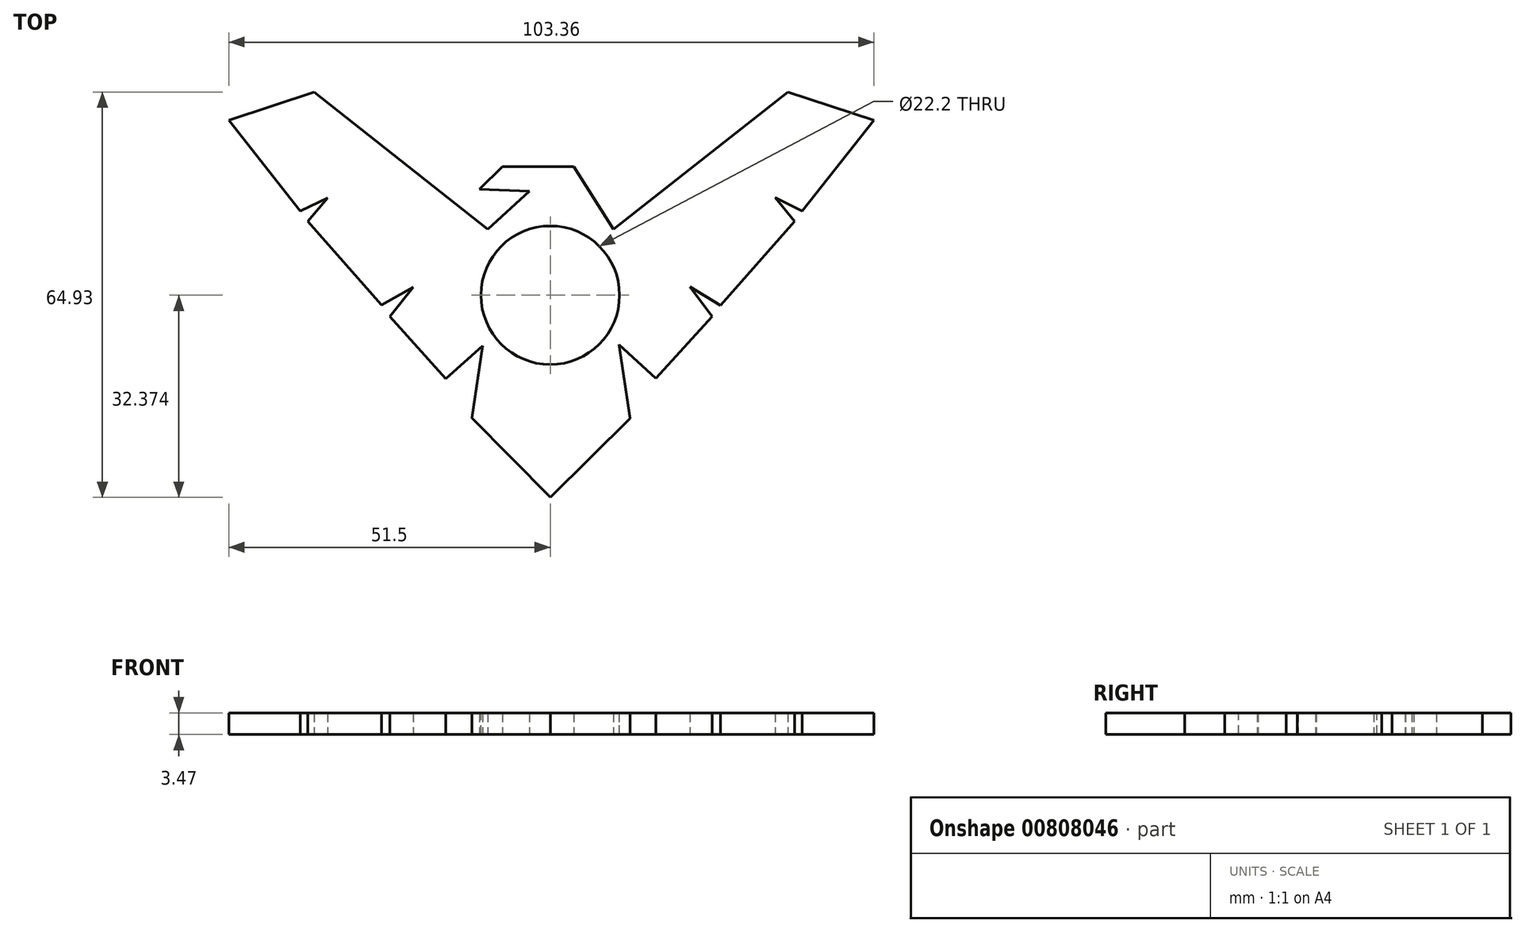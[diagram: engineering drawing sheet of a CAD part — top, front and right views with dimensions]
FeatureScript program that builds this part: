
annotation { "Feature Type Name" : "Feature", "Feature Type Description" : "" }
export const myFeature = defineFeature(function(context is Context, id is Id, definition is map)
    precondition{}
    {
        {
            var Q0;
            Q0=qCreatedBy(makeId("Top.planeOp"),FACE);
            var sketch = newSketch(context, id + "F0", { "sketchPlane" : qUnion([Q0])});
            skLineSegment(sketch, "E0", {"start": v(-103, 52.46) * mm, "end": v(-75.69, 61.5) * mm});
            skLineSegment(sketch, "E1", {"start": v(-75.69, 61.5) * mm, "end": v(-20, 17.53) * mm});
            skLineSegment(sketch, "E2", {"start": v(-20, 17.53) * mm, "end": v(-6.7, 29.72) * mm});
            skLineSegment(sketch, "E3", {"start": v(-6.7, 29.72) * mm, "end": v(-22.67, 30.32) * mm});
            skLineSegment(sketch, "E4", {"start": v(-22.67, 30.32) * mm, "end": v(-15.35, 37.57) * mm});
            skLineSegment(sketch, "E5", {"start": v(-15.35, 37.57) * mm, "end": v(7.55, 37.57) * mm});
            skLineSegment(sketch, "E6", {"start": v(7.55, 37.57) * mm, "end": v(20.27, 17.53) * mm});
            skLineSegment(sketch, "E7", {"start": v(20.27, 17.53) * mm, "end": v(76.07, 61.5) * mm});
            skLineSegment(sketch, "E8", {"start": v(76.07, 61.5) * mm, "end": v(103.73, 52.38) * mm});
            skLineSegment(sketch, "E9", {"start": v(103.73, 52.38) * mm, "end": v(80.74, 23.35) * mm});
            skLineSegment(sketch, "E10", {"start": v(80.74, 23.35) * mm, "end": v(72.05, 27.7) * mm});
            skLineSegment(sketch, "E11", {"start": v(72.05, 27.7) * mm, "end": v(78.23, 20.1) * mm});
            skLineSegment(sketch, "E12", {"start": v(78.23, 20.1) * mm, "end": v(54.59, -6.93) * mm});
            skLineSegment(sketch, "E13", {"start": v(54.59, -6.93) * mm, "end": v(44.76, -0.93) * mm});
            skLineSegment(sketch, "E14", {"start": v(44.76, -0.93) * mm, "end": v(51.93, -10.47) * mm});
            skLineSegment(sketch, "E15", {"start": v(51.93, -10.47) * mm, "end": v(33.89, -30.25) * mm});
            skLineSegment(sketch, "E16", {"start": v(33.89, -30.25) * mm, "end": v(22.08, -19.48) * mm});
            skLineSegment(sketch, "E17", {"start": v(22.08, -19.48) * mm, "end": v(25.62, -43.04) * mm});
            skLineSegment(sketch, "E18", {"start": v(25.62, -43.04) * mm, "end": v(0, -68.37) * mm});
            skLineSegment(sketch, "E19", {"start": v(0, -68.37) * mm, "end": v(-25.13, -42.95) * mm});
            skLineSegment(sketch, "E20", {"start": v(-25.13, -42.95) * mm, "end": v(-21.72, -19.79) * mm});
            skLineSegment(sketch, "E21", {"start": v(-21.72, -19.79) * mm, "end": v(-33.51, -30.3) * mm});
            skLineSegment(sketch, "E22", {"start": v(-33.51, -30.3) * mm, "end": v(-51.44, -10.47) * mm});
            skLineSegment(sketch, "E23", {"start": v(-51.44, -10.47) * mm, "end": v(-43.96, -1.07) * mm});
            skLineSegment(sketch, "E24", {"start": v(-43.96, -1.07) * mm, "end": v(-54.02, -6.76) * mm});
            skLineSegment(sketch, "E25", {"start": v(-54.02, -6.76) * mm, "end": v(-77.73, 20.04) * mm});
            skLineSegment(sketch, "E26", {"start": v(-77.73, 20.04) * mm, "end": v(-71.33, 27.57) * mm});
            skLineSegment(sketch, "E27", {"start": v(-71.33, 27.57) * mm, "end": v(-80.06, 23.35) * mm});
            skLineSegment(sketch, "E28", {"start": v(-80.06, 23.35) * mm, "end": v(-103, 52.46) * mm});
            skSolve(sketch);
        }
        {
            var Q0;
            Q0 = qSketchRegion(id + "F0", true);
            extrude(context, id + "F1", {"entities" : qUnion([Q0]), "depth" : 6.93 * mm, "offsetDistance" : 25.4 * mm});
        }
        {
            var Q0;
            Q0=makeQuery(id+"F1.opExtrude","SWEPT_BODY",BODY,{"disambiguationData":[OSD([sQuery(id+"F0.wireOp",EDGE,"E0"),sQuery(id+"F0.wireOp",EDGE,"E1"),sQuery(id+"F0.wireOp",EDGE,"E2"),sQuery(id+"F0.wireOp",EDGE,"E3"),sQuery(id+"F0.wireOp",EDGE,"E4"),sQuery(id+"F0.wireOp",EDGE,"E5"),sQuery(id+"F0.wireOp",EDGE,"E6"),sQuery(id+"F0.wireOp",EDGE,"E7"),sQuery(id+"F0.wireOp",EDGE,"E8"),sQuery(id+"F0.wireOp",EDGE,"E9"),sQuery(id+"F0.wireOp",EDGE,"E10"),sQuery(id+"F0.wireOp",EDGE,"E11"),sQuery(id+"F0.wireOp",EDGE,"E12"),sQuery(id+"F0.wireOp",EDGE,"E13"),sQuery(id+"F0.wireOp",EDGE,"E14"),sQuery(id+"F0.wireOp",EDGE,"E15"),sQuery(id+"F0.wireOp",EDGE,"E16"),sQuery(id+"F0.wireOp",EDGE,"E17"),sQuery(id+"F0.wireOp",EDGE,"E18"),sQuery(id+"F0.wireOp",EDGE,"E19"),sQuery(id+"F0.wireOp",EDGE,"E20"),sQuery(id+"F0.wireOp",EDGE,"E21"),sQuery(id+"F0.wireOp",EDGE,"E22"),sQuery(id+"F0.wireOp",EDGE,"E23"),sQuery(id+"F0.wireOp",EDGE,"E24"),sQuery(id+"F0.wireOp",EDGE,"E25"),sQuery(id+"F0.wireOp",EDGE,"E26"),sQuery(id+"F0.wireOp",EDGE,"E27"),sQuery(id+"F0.wireOp",EDGE,"E28"),sQuery(id+"F0.wireOp",EDGE,"hpiGP7Qw-26ds-mfYW-nCt3-OEcmAq7lWbwC")])]});
            var Q1;
            Q1=qCreatedBy(makeId("Origin.pointOp"),VERTEX);
            var Q2;
            Q2=qCreatedBy(makeId("Origin.pointOp"),VERTEX);
            transform(context, id + "F2", {"entities" : qUnion([Q0]), "transformType" : TransformType.SCALE_UNIFORMLY, "scale" : .5, "scalePoint" : qUnion([Q2]), "makeCopy" : false});
        }
        {
            var Q0;
            Q0=makeQuery(id+"F1.opExtrude","CAP_FACE",FACE,{"disambiguationData":[OSD([sQuery(id+"F0.wireOp",EDGE,"E0"),sQuery(id+"F0.wireOp",EDGE,"E1"),sQuery(id+"F0.wireOp",EDGE,"E2"),sQuery(id+"F0.wireOp",EDGE,"E3"),sQuery(id+"F0.wireOp",EDGE,"E4"),sQuery(id+"F0.wireOp",EDGE,"E5"),sQuery(id+"F0.wireOp",EDGE,"E6"),sQuery(id+"F0.wireOp",EDGE,"E7"),sQuery(id+"F0.wireOp",EDGE,"E8"),sQuery(id+"F0.wireOp",EDGE,"E9"),sQuery(id+"F0.wireOp",EDGE,"E10"),sQuery(id+"F0.wireOp",EDGE,"E11"),sQuery(id+"F0.wireOp",EDGE,"E12"),sQuery(id+"F0.wireOp",EDGE,"E13"),sQuery(id+"F0.wireOp",EDGE,"E14"),sQuery(id+"F0.wireOp",EDGE,"E15"),sQuery(id+"F0.wireOp",EDGE,"E16"),sQuery(id+"F0.wireOp",EDGE,"E17"),sQuery(id+"F0.wireOp",EDGE,"E18"),sQuery(id+"F0.wireOp",EDGE,"E19"),sQuery(id+"F0.wireOp",EDGE,"E20"),sQuery(id+"F0.wireOp",EDGE,"E21"),sQuery(id+"F0.wireOp",EDGE,"E22"),sQuery(id+"F0.wireOp",EDGE,"E23"),sQuery(id+"F0.wireOp",EDGE,"E24"),sQuery(id+"F0.wireOp",EDGE,"E25"),sQuery(id+"F0.wireOp",EDGE,"E26"),sQuery(id+"F0.wireOp",EDGE,"E27"),sQuery(id+"F0.wireOp",EDGE,"E28"),sQuery(id+"F0.wireOp",EDGE,"hpiGP7Qw-26ds-mfYW-nCt3-OEcmAq7lWbwC")])],"isStart":false});
            var sketch = newSketch(context, id + "F3", { "sketchPlane" : qUnion([Q0])});
            skCircle(sketch, "E29", {"center": v(0, -1.8) * mm, "radius": 11.1 * mm});
            skSolve(sketch);
        }
        {
            var Q0;
            Q0=makeQuery(id+"F3.imprint","IMPRINT",FACE,{"disambiguationData":[TD([[makeQuery(id+"F3.imprint","IMPRINT",EDGE,{"derivedFrom":sQuery(id+"F3.wireOp",EDGE,"E29")}),1.0]])]});
            extrude(context, id + "F4", {"entities" : qUnion([Q0]), "operationType" : NewBodyOperationType.REMOVE, "oppositeDirection" : true, "depth" : 25.4 * mm, "offsetDistance" : 25.4 * mm});
        }
    });
